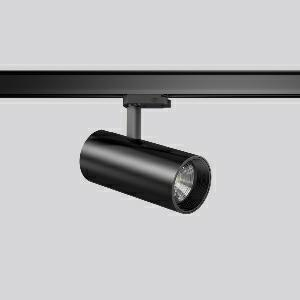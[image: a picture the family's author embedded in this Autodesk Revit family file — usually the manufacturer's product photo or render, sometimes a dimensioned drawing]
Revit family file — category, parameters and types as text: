
# Revit family: deecos_s_mini_742207_003_3_07da
name_source: partatom
category: Lighting Fixtures
units: mm (PartAtom-declared; Revit-internal decimal feet)

## family parameters
Cut with Voids When Loaded = No
Host = Face
Light Source = No
Part Type = Normal
Room Calculation Point = No
Round Connector Dimension = Use Diameter
Shared = No

## types (1)
- DEECOS S mini (1 x LED Modul 935, 3050 lm, 3500)
    Apparent Load = 29 VA
    Approval mark = CE
    CIE Flux Codes = 96 100 100 100 100
    Color Rendering = 92
    Color Temperature = 3500
    Default Elevation = 1800 mm
    Description = Series: DEECOS S mini
LED surface-mounted projector in modern design with no visible cooling ribs. Housing: die-cast aluminium, powder-coated. Rotation range: 356°. Swivel range: 90°. Black plastic ring and recessed LED to prevent glare from the side. Optical assembly with lens made of plastic (polycarbonate) for the best homogeneous light distribution - can be changed without tools. Best colour rendering index Ra>90. With multi adaptor for 3-circuit tracks 230 V. Suitable for Track on ceiling, Wall track. High quality converter without flickering and stroboscopic effect. The following accessories can be mounted without use of tools: interchangeable lenses, decorative glasses, honeycomb louvre, clear and frosted diffusers, white interchangeable plastic ring. 
Colour: deep black, matt (RAL 9005)
Diameter: 87 mm
Height: 214 mm
Lamp: LED
Socket: without socket
Colour temperature: 3500K
Colour rendering index (CRI): 92
System power: 29 W
Rated luminous flux: 3050 lm
Luminous efficiency: 105 lm/W
Control gear: Regulated power supply
Protection class: I
Type of protection: IP 20
    Height = 214 mm
    Lamp = 1 x LED Modul 935
    Lamp Light Flux = 3050 lm
    Lamp count = 1
    Length = 87 mm
    Lifetime = 50000 h
    Luminous efficacy = 105 lm/W
    Manufacturer = RZB
    ModVariant = No
    Model = 742207.003.3
    Mounting Place = Ceiling
    Mounting Type = Rail mounted
    Number of Poles = 1
    OnlyDefault = Yes
    Power Factor = 1
    Product Name = DEECOS S mini
    Product group = Track mounted projectors
    ProductGroupID = 301
    Protection Class = Protection class I
    Protection Degree = IP 20
    RLX_Detail_Level = 1
    RLX_Emergency_Light_Flux = 0 lm
    RLX_Emergency_Type = 0
    RLX_Emergency_Type_DB = No
    RlxData = <blob elided: 38849 chars, md5=a309f07c>
    Socket = socket
    Standby Power = 0 W
    System Light Flux = 3050 lm
    System Power = 29 W
    Type Comments = Product without accessories
    Type Image = 741930.003.jpg
    URL = http://relux.com
    VarID = ---
    Voltage = 230 V
    Voltage Range = 220-240 V
    Weight = 0.00 kg
    Width = 0 mm  [stored 0 ft]

note: [stored X ft] marks values corroborated as IEEE doubles in the binary element streams (Revit-internal decimal feet)

## geometry (parser evidence)
native form markers: Blend x4, Sweep x12
no freeform markers — native parametric forms only
